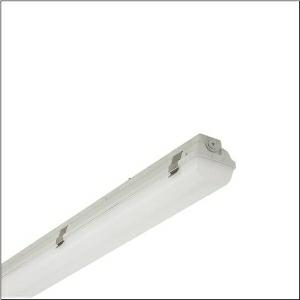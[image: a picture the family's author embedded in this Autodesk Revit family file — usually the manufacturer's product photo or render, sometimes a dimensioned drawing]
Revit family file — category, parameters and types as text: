
# Revit family: monsun_r__21_eco_51fj10dp47a_8000
name_source: partatom
category: Lighting Fixtures
units: mm (PartAtom-declared; Revit-internal decimal feet)

## family parameters
Cut with Voids When Loaded = No
Host = Face
Light Source = No
Part Type = Normal
Room Calculation Point = No
Round Connector Dimension = Use Diameter
Shared = No

## types (1)
- Monsun® 21 Eco (1 x LED, 7000 lm, 50 W, 4000K)
    Apparent Load = 50 VA
    CIE Flux Codes = 41 70 89 90 100
    Color Rendering = 80
    Color Temperature = 4000K
    Default Elevation = 1800 mm
    Description = Monsun® 21 Eco, damp-proof luminaire, primary optical cover: diffuser, of PMMA, frosted, light emission: direct distribution, primary light characteristic: symmetric, installation type: suspended mounting, surface-mounted, LED, rated luminous flux: 7.000lm, luminous efficacy: 140lm/W, light colour: 840, colour temperature: 4000K, control gear: DALI, with terminal, 5-pole, max. 2.5mm², mains connection: 220..240V, AC, 50/60Hz, rated input power: 50W, housing, of glass-fibre reinforced polyester, light grey (RAL 7035), length: 1.577mm, width: 90mm, height: 95mm, clip for enclosure, of spring steel V2A, protection rating (complete): IP66, insulation class (complete): insulation class I (protective earthing), certification: CE, UKCA, protection symbol: D, impact resistance: IK02, permissible operating ambient temperature: -20..+35°C, corresponds to IFS (International Featured Standards) requirements for safety and quality in the food industry, contact your sales advisor before using the luminaires in applications with unclear chemical exposure, large temperature fluctuations or condensation-forming humidity, packaging unit: 1 piece
    Height = 103 mm
    Lamp = 1 x LED
    Lamp Light Flux = 7000 lm
    Lamp Power = 50 W
    Lamp count = 1
    Length = 1577 mm
    Luminous efficacy = 140 lm/W
    Manufacturer = Siteco
    ModVariant = No
    Model = 51FJ10DP47A
    Mounting Place = Ceiling
    Mounting Type = Surface mounted
    Number of Poles = 1
    OnlyDefault = Yes
    Power Factor = 1
    Product Name = Monsun® 21 Eco
    Product group = damp-proof luminaire
    ProductGroupID = 300
    Protection Class = Protection class I
    Protection Degree = IP 66
    RLX_Detail_Level = 1
    RLX_Emergency_Light_Flux = 0 lm
    RLX_Emergency_Type = 0
    RLX_Emergency_Type_DB = No
    RlxData = <blob elided: 33481 chars, md5=6fa8f88b>
    Socket = socket
    Standby Power = 0 W
    System Light Flux = 7000 lm
    System Power = 50 W
    Type Comments = Product without accessories
    Type Image = l_1007218.jpg
    URL = http://relux.com
    VarID = ---
    Voltage = 0 V
    Weight = 0.00 kg
    Width = 90 mm

## geometry (parser evidence)
native form markers: Blend x4, Sweep x12
no freeform markers — native parametric forms only
